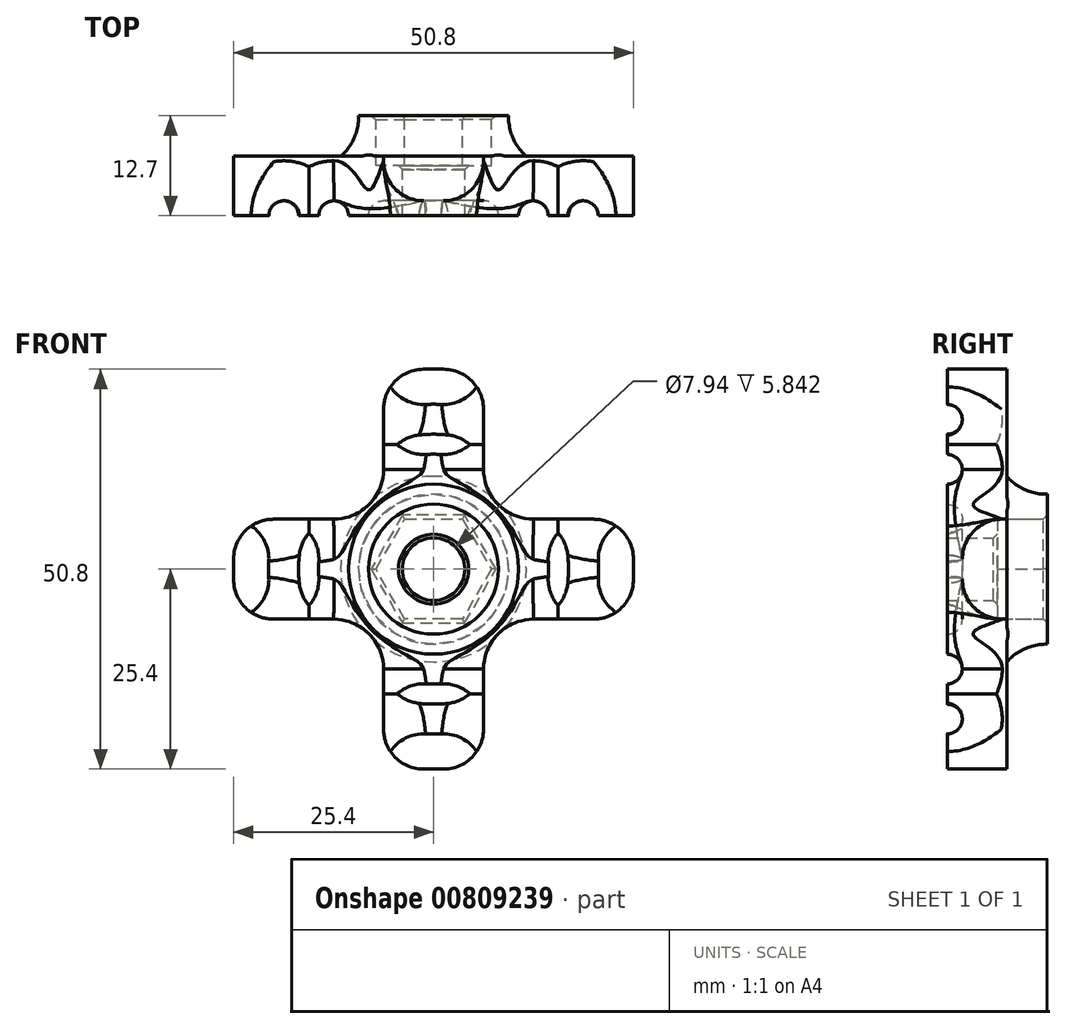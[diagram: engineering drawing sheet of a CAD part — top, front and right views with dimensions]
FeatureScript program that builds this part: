
annotation { "Feature Type Name" : "Feature", "Feature Type Description" : "" }
export const myFeature = defineFeature(function(context is Context, id is Id, definition is map)
    precondition{}
    {
        {
            var Q0;
            Q0=qCreatedBy(makeId("Front.planeOp"),FACE);
            var sketch = newSketch(context, id + "F0", { "sketchPlane" : qUnion([Q0])});
            skCircle(sketch, "E0.cCircle", {"center": v(0, 0) * mm, "radius": 6.35 * mm, "construction": true});
            skLineSegment(sketch, "E0.0", {"start": v(-3.67, 6.35) * mm, "end": v(3.67, 6.35) * mm});
            skLineSegment(sketch, "E0.1", {"start": v(3.67, 6.35) * mm, "end": v(7.33, 0) * mm});
            skLineSegment(sketch, "E0.2", {"start": v(7.33, 0) * mm, "end": v(3.67, -6.35) * mm});
            skLineSegment(sketch, "E0.3", {"start": v(3.67, -6.35) * mm, "end": v(-3.67, -6.35) * mm});
            skLineSegment(sketch, "E0.4", {"start": v(-3.67, -6.35) * mm, "end": v(-7.33, 0) * mm});
            skLineSegment(sketch, "E0.5", {"start": v(-7.33, 0) * mm, "end": v(-3.67, 6.35) * mm});
            skPoint(sketch, "E0.0.midPoint", {"position": v(0, 6.35) * mm});
            skCircle(sketch, "E1", {"center": v(0, 0) * mm, "radius": 3.97 * mm});
            skSolve(sketch);
        }
        {
            var Q0;
            Q0 = qSketchRegion(id + "F0", true);
            extrude(context, id + "F1", {"entities" : qUnion([Q0]), "depth" : 6.35 * mm, "offsetDistance" : 25.4 * mm});
        }
        {
            var Q0;
            Q0=qCreatedBy(makeId("Front.planeOp"),FACE);
            var sketch = newSketch(context, id + "F2", { "sketchPlane" : qUnion([Q0])});
            skLineSegment(sketch, "E2.0.0", {"start": v(-3.67, 6.35) * mm, "end": v(-7.33, 0) * mm});
            skLineSegment(sketch, "E2.0.1", {"start": v(-7.33, 0) * mm, "end": v(-3.67, -6.35) * mm});
            skLineSegment(sketch, "E2.0.2", {"start": v(-3.67, -6.35) * mm, "end": v(3.67, -6.35) * mm});
            skLineSegment(sketch, "E2.0.4", {"start": v(7.33, 0) * mm, "end": v(3.67, 6.35) * mm});
            skLineSegment(sketch, "E2.0.5", {"start": v(3.67, 6.35) * mm, "end": v(-3.67, 6.35) * mm});
            skLineSegment(sketch, "E3", {"start": v(-12.7, 6.35) * mm, "end": v(-20.32, 6.35) * mm});
            skLineSegment(sketch, "E4.MirrorCS", {"start": v(-12.7, -6.35) * mm, "end": v(-20.32, -6.35) * mm});
            skLineSegment(sketch, "E5.MirrorCS", {"start": v(12.7, 6.35) * mm, "end": v(20.32, 6.35) * mm});
            skLineSegment(sketch, "E6.MirrorCS", {"start": v(12.7, -6.35) * mm, "end": v(20.32, -6.35) * mm});
            skLineSegment(sketch, "E7", {"start": v(-6.35, 12.7) * mm, "end": v(-6.35, 20.32) * mm});
            skLineSegment(sketch, "E8.MirrorCS", {"start": v(6.35, 12.7) * mm, "end": v(6.35, 20.32) * mm});
            skLineSegment(sketch, "E9.MirrorCS", {"start": v(-6.35, -12.7) * mm, "end": v(-6.35, -20.32) * mm});
            skLineSegment(sketch, "E10.MirrorCS", {"start": v(6.35, -12.7) * mm, "end": v(6.35, -20.32) * mm});
            skLineSegment(sketch, "E11", {"start": v(-1.27, 25.4) * mm, "end": v(1.27, 25.4) * mm});
            skLineSegment(sketch, "E12", {"start": v(25.4, 1.27) * mm, "end": v(25.4, -1.27) * mm});
            skLineSegment(sketch, "E13", {"start": v(-25.4, 1.27) * mm, "end": v(-25.4, -1.27) * mm});
            skLineSegment(sketch, "E14", {"start": v(-1.27, -25.4) * mm, "end": v(1.27, -25.4) * mm});
            skArc(sketch, "E15", {"start": v(-6.35, -12.7) * mm, "mid": v(-8.2, -8.2) * mm, "end": v(-12.7, -6.35) * mm});
            skArc(sketch, "E16", {"start": v(-12.7, 6.35) * mm, "mid": v(-8.2, 8.2) * mm, "end": v(-6.35, 12.7) * mm});
            skArc(sketch, "E17", {"start": v(6.35, 12.7) * mm, "mid": v(8.2, 8.2) * mm, "end": v(12.7, 6.35) * mm});
            skArc(sketch, "E18", {"start": v(12.7, -6.35) * mm, "mid": v(8.2, -8.2) * mm, "end": v(6.35, -12.7) * mm});
            skPoint(sketch, "E19.MirrorCS.start.orphan", {"position": v(0, 12.7) * mm});
            skLineSegment(sketch, "E20.0.3", {"start": v(3.67, -6.35) * mm, "end": v(7.33, 0) * mm});
            skPoint(sketch, "E21.visualSharp", {"position": v(-25.4, 6.35) * mm});
            skArc(sketch, "E21.filletArc", {"start": v(-20.32, 6.35) * mm, "mid": v(-23.91, 4.86) * mm, "end": v(-25.4, 1.27) * mm});
            skPoint(sketch, "E22.visualSharp", {"position": v(-25.4, -6.35) * mm});
            skArc(sketch, "E22.filletArc", {"start": v(-25.4, -1.27) * mm, "mid": v(-23.91, -4.86) * mm, "end": v(-20.32, -6.35) * mm});
            skPoint(sketch, "E23.visualSharp", {"position": v(-6.35, -25.4) * mm});
            skArc(sketch, "E23.filletArc", {"start": v(-6.35, -20.32) * mm, "mid": v(-4.86, -23.91) * mm, "end": v(-1.27, -25.4) * mm});
            skPoint(sketch, "E24.visualSharp", {"position": v(6.35, -25.4) * mm});
            skArc(sketch, "E24.filletArc", {"start": v(1.27, -25.4) * mm, "mid": v(4.86, -23.91) * mm, "end": v(6.35, -20.32) * mm});
            skPoint(sketch, "E25.visualSharp", {"position": v(25.4, -6.35) * mm});
            skArc(sketch, "E25.filletArc", {"start": v(20.32, -6.35) * mm, "mid": v(23.91, -4.86) * mm, "end": v(25.4, -1.27) * mm});
            skPoint(sketch, "E26.visualSharp", {"position": v(25.4, 6.35) * mm});
            skArc(sketch, "E26.filletArc", {"start": v(25.4, 1.27) * mm, "mid": v(23.91, 4.86) * mm, "end": v(20.32, 6.35) * mm});
            skPoint(sketch, "E27.visualSharp", {"position": v(6.35, 25.4) * mm});
            skArc(sketch, "E27.filletArc", {"start": v(6.35, 20.32) * mm, "mid": v(4.86, 23.91) * mm, "end": v(1.27, 25.4) * mm});
            skPoint(sketch, "E28.visualSharp", {"position": v(-6.35, 25.4) * mm});
            skArc(sketch, "E28.filletArc", {"start": v(-1.27, 25.4) * mm, "mid": v(-4.86, 23.91) * mm, "end": v(-6.35, 20.32) * mm});
            skSolve(sketch);
        }
        {
            var Q0;
            Q0 = qSketchRegion(id + "F2", true);
            extrude(context, id + "F3", {"entities" : qUnion([Q0]), "operationType" : NewBodyOperationType.ADD, "depth" : 6.35 * mm, "offsetDistance" : 25.4 * mm, "hasSecondDirection" : true, "secondDirectionOppositeDirection" : true, "secondDirectionDepth" : 6.35 * mm});
        }
        {
            var Q0;
            Q0=qCreatedBy(makeId("Right.planeOp"),FACE);
            var sketch = newSketch(context, id + "F4", { "sketchPlane" : qUnion([Q0])});
            skPoint(sketch, "E29.0", {"position": v(-6.35, 6.35) * mm});
            skLineSegment(sketch, "E30.0", {"start": v(-6.35, 6.35) * mm, "end": v(-6.35, 12.7) * mm});
            skLineSegment(sketch, "E31.0", {"start": v(-6.35, 12.7) * mm, "end": v(-6.35, 20.32) * mm});
            skLineSegment(sketch, "E32.0", {"start": v(-6.35, 25.4) * mm, "end": v(-6.35, 20.32) * mm});
            skLineSegment(sketch, "E33.0", {"start": v(-6.35, 25.4) * mm, "end": v(6.35, 25.4) * mm});
            skPoint(sketch, "E34.0", {"position": v(-6.35, 0) * mm});
            skLineSegment(sketch, "E35.bottom", {"start": v(0, 25.4) * mm, "end": v(-6.35, 25.4) * mm});
            skLineSegment(sketch, "E35.top", {"start": v(0, 0) * mm, "end": v(-4.45, 0) * mm});
            skLineSegment(sketch, "E35.right", {"start": v(-6.35, 25.4) * mm, "end": v(-6.35, 0) * mm});
            skLineSegment(sketch, "E36.0", {"start": v(-4.45, 19.05) * mm, "end": v(6.35, 19.05) * mm});
            skArc(sketch, "E37", {"start": v(-6.35, 17.15) * mm, "mid": v(-4.45, 19.05) * mm, "end": v(-6.35, 20.96) * mm});
            skArc(sketch, "E38", {"start": v(-6.35, 10.8) * mm, "mid": v(-4.45, 12.7) * mm, "end": v(-6.35, 14.6) * mm});
            skArc(sketch, "E39", {"start": v(-6.35, 4.45) * mm, "mid": v(-4.45, 6.35) * mm, "end": v(-6.35, 8.26) * mm});
            skPoint(sketch, "E40.0", {"position": v(-6.35, 1.27) * mm});
            skCircle(sketch, "E41", {"center": v(-6.35, 0) * mm, "radius": 1.9 * mm});
            skLineSegment(sketch, "E42", {"start": v(-6.35, 20.96) * mm, "end": v(-6.35, -1.9) * mm});
            skSolve(sketch);
        }
        {
            var Q0;
            {var subQ0=sQuery(id+"F4.wireOp",EDGE,"E38");Q0=makeQuery(id+"F4.imprint","IMPRINT",FACE,{"disambiguationData":[TD([[makeQuery(id+"F4.imprint","IMPRINT",EDGE,{"derivedFrom":subQ0}),1.0]])]});}
            var Q1;
            {var subQ0=sQuery(id+"F4.wireOp",EDGE,"E37");var subQ1=makeQuery(id+"F4.imprint","IMPRINT",VERTEX,{"derivedFrom":subQ0});Q1=makeQuery(id+"F4.imprint","IMPRINT",FACE,{"disambiguationData":[TD([[makeQuery(id+"F4.imprint","IMPRINT",EDGE,{"disambiguationData":[TD([[subQ1,1.0]])],"derivedFrom":subQ0}),1.0]])]});}
            var Q2;
            {var subQ0=sQuery(id+"F4.wireOp",EDGE,"E39");Q2=makeQuery(id+"F4.imprint","IMPRINT",FACE,{"disambiguationData":[TD([[makeQuery(id+"F4.imprint","IMPRINT",EDGE,{"derivedFrom":subQ0}),1.0]])]});}
            var Q3;
            Q3=sQuery(id+"F4.wireOp",EDGE,"E35.top");
            revolve(context, id + "F5", {"operationType" : NewBodyOperationType.REMOVE, "surfaceOperationType" : NewSurfaceOperationType.NEW, "entities" : qUnion([Q0, Q1, Q2]), "axis" : qUnion([Q3]), "revolveType" : RevolveType.FULL});
        }
        {
            var Q0;
            Q0=qCreatedBy(makeId("Top.planeOp"),FACE);
            var sketch = newSketch(context, id + "F6", { "sketchPlane" : qUnion([Q0])});
            skPoint(sketch, "E43.0", {"position": v(12.7, 6.35) * mm});
            skLineSegment(sketch, "E44.0", {"start": v(25.4, 1.21) * mm, "end": v(25.4, 6.35) * mm});
            skLineSegment(sketch, "E45.0", {"start": v(12.7, 6.35) * mm, "end": v(20.32, 6.35) * mm});
            skLineSegment(sketch, "E46.0", {"start": v(12.7, 6.35) * mm, "end": v(6.35, 6.35) * mm});
            skLineSegment(sketch, "E47.0.1", {"start": v(6.35, -5.17) * mm, "end": v(6.35, 6.35) * mm});
            skLineSegment(sketch, "E47.0.2", {"start": v(6.35, 6.35) * mm, "end": v(12.7, 6.35) * mm});
            skArc(sketch, "E48", {"start": v(9.52, 6.35) * mm, "mid": v(10.09, 3.53) * mm, "end": v(11.79, 1.21) * mm});
            skLineSegment(sketch, "E49", {"start": v(11.79, 1.21) * mm, "end": v(25.4, 1.21) * mm});
            skLineSegment(sketch, "E50", {"start": v(9.52, 6.35) * mm, "end": v(25.4, 6.35) * mm});
            skPoint(sketch, "E51.orphan", {"position": v(25.4, -6.35) * mm});
            skLineSegment(sketch, "E52.bottom", {"start": v(25.4, 1.21) * mm, "end": v(30.77, 1.21) * mm});
            skLineSegment(sketch, "E52.top", {"start": v(25.4, 9.12) * mm, "end": v(30.77, 9.12) * mm});
            skLineSegment(sketch, "E52.left", {"start": v(25.4, 1.21) * mm, "end": v(25.4, 9.12) * mm});
            skLineSegment(sketch, "E52.right", {"start": v(30.77, 1.21) * mm, "end": v(30.77, 9.12) * mm});
            skSolve(sketch);
        }
        {
            var Q0;
            {var subQ0=sQuery(id+"F6.wireOp",EDGE,"E48");Q0=makeQuery(id+"F6.imprint","IMPRINT",FACE,{"disambiguationData":[TD([[makeQuery(id+"F6.imprint","IMPRINT",EDGE,{"derivedFrom":subQ0}),1.0]])]});}
            var Q1;
            {var subQ3=sQuery(id+"F6.wireOp",EDGE,"E52.bottom");Q1=makeQuery(id+"F6.imprint","IMPRINT",FACE,{"disambiguationData":[TD([[makeQuery(id+"F6.imprint","IMPRINT",EDGE,{"derivedFrom":subQ3}),1.0]])]});}
            var Q2;
            Q2=makeQuery(id+"F1.opExtrude","SWEPT_FACE",FACE,{"disambiguationData":[OSD([sQuery(id+"F0.wireOp",EDGE,"E1")])]});
            revolve(context, id + "F7", {"operationType" : NewBodyOperationType.REMOVE, "surfaceOperationType" : NewSurfaceOperationType.NEW, "entities" : qUnion([Q0, Q1]), "axis" : qUnion([Q2]), "revolveType" : RevolveType.FULL});
        }
        {
            var Q0;
            Q0=makeQuery(id+"F5.boolean.opBoolean","INTERSECT",EDGE,{"derivedFrom":[makeQuery(id+"F3.opExtrude","SWEPT_FACE",FACE,{"disambiguationData":[OSD([sQuery(id+"F2.wireOp",EDGE,"E6.MirrorCS")])]}),makeQuery(id+"F5.opRevolve","SWEPT_FACE",FACE,{"disambiguationData":[OSD([sQuery(id+"F4.wireOp",EDGE,"E37")])]})]});
            var Q1;
            Q1=makeQuery(id+"F5.boolean.opBoolean","INTERSECT",EDGE,{"derivedFrom":[makeQuery(id+"F3.opExtrude","SWEPT_FACE",FACE,{"disambiguationData":[OSD([sQuery(id+"F2.wireOp",EDGE,"E5.MirrorCS")])]}),makeQuery(id+"F5.opRevolve","SWEPT_FACE",FACE,{"disambiguationData":[OSD([sQuery(id+"F4.wireOp",EDGE,"E37")])]})]});
            var Q2;
            Q2=makeQuery(id+"F5.boolean.opBoolean","INTERSECT",EDGE,{"derivedFrom":[makeQuery(id+"F3.opExtrude","SWEPT_FACE",FACE,{"disambiguationData":[OSD([sQuery(id+"F2.wireOp",EDGE,"E18")])]}),makeQuery(id+"F5.opRevolve","SWEPT_FACE",FACE,{"disambiguationData":[OSD([sQuery(id+"F4.wireOp",EDGE,"E38")])]})]});
            var Q3;
            Q3=makeQuery(id+"F5.boolean.opBoolean","INTERSECT",EDGE,{"derivedFrom":[makeQuery(id+"F3.opExtrude","SWEPT_FACE",FACE,{"disambiguationData":[OSD([sQuery(id+"F2.wireOp",EDGE,"E17")])]}),makeQuery(id+"F5.opRevolve","SWEPT_FACE",FACE,{"disambiguationData":[OSD([sQuery(id+"F4.wireOp",EDGE,"E38")])]})]});
            var Q4;
            Q4=makeQuery(id+"F5.boolean.opBoolean","INTERSECT",EDGE,{"derivedFrom":[makeQuery(id+"F3.opExtrude","SWEPT_FACE",FACE,{"disambiguationData":[OSD([sQuery(id+"F2.wireOp",EDGE,"E15")])]}),makeQuery(id+"F5.opRevolve","SWEPT_FACE",FACE,{"disambiguationData":[OSD([sQuery(id+"F4.wireOp",EDGE,"E38")])]})]});
            var Q5;
            Q5=makeQuery(id+"F5.boolean.opBoolean","INTERSECT",EDGE,{"derivedFrom":[makeQuery(id+"F3.opExtrude","SWEPT_FACE",FACE,{"disambiguationData":[OSD([sQuery(id+"F2.wireOp",EDGE,"E4.MirrorCS")])]}),makeQuery(id+"F5.opRevolve","SWEPT_FACE",FACE,{"disambiguationData":[OSD([sQuery(id+"F4.wireOp",EDGE,"E37")])]})]});
            var Q6;
            Q6=makeQuery(id+"F5.boolean.opBoolean","INTERSECT",EDGE,{"derivedFrom":[makeQuery(id+"F3.opExtrude","SWEPT_FACE",FACE,{"disambiguationData":[OSD([sQuery(id+"F2.wireOp",EDGE,"E3")])]}),makeQuery(id+"F5.opRevolve","SWEPT_FACE",FACE,{"disambiguationData":[OSD([sQuery(id+"F4.wireOp",EDGE,"E37")])]})]});
            var Q7;
            Q7=makeQuery(id+"F5.boolean.opBoolean","INTERSECT",EDGE,{"derivedFrom":[makeQuery(id+"F3.opExtrude","SWEPT_FACE",FACE,{"disambiguationData":[OSD([sQuery(id+"F2.wireOp",EDGE,"E7")])]}),makeQuery(id+"F5.opRevolve","SWEPT_FACE",FACE,{"disambiguationData":[OSD([sQuery(id+"F4.wireOp",EDGE,"E37")])]})]});
            var Q8;
            Q8=makeQuery(id+"F5.boolean.opBoolean","INTERSECT",EDGE,{"derivedFrom":[makeQuery(id+"F3.opExtrude","SWEPT_FACE",FACE,{"disambiguationData":[OSD([sQuery(id+"F2.wireOp",EDGE,"E8.MirrorCS")])]}),makeQuery(id+"F5.opRevolve","SWEPT_FACE",FACE,{"disambiguationData":[OSD([sQuery(id+"F4.wireOp",EDGE,"E37")])]})]});
            var Q9;
            Q9=makeQuery(id+"F5.boolean.opBoolean","INTERSECT",EDGE,{"derivedFrom":[makeQuery(id+"F3.opExtrude","SWEPT_FACE",FACE,{"disambiguationData":[OSD([sQuery(id+"F2.wireOp",EDGE,"E16")])]}),makeQuery(id+"F5.opRevolve","SWEPT_FACE",FACE,{"disambiguationData":[OSD([sQuery(id+"F4.wireOp",EDGE,"E38")])]})]});
            var Q10;
            Q10=makeQuery(id+"F5.boolean.opBoolean","INTERSECT",EDGE,{"derivedFrom":[makeQuery(id+"F3.opExtrude","SWEPT_FACE",FACE,{"disambiguationData":[OSD([sQuery(id+"F2.wireOp",EDGE,"E9.MirrorCS")])]}),makeQuery(id+"F5.opRevolve","SWEPT_FACE",FACE,{"disambiguationData":[OSD([sQuery(id+"F4.wireOp",EDGE,"E37")])]})]});
            var Q11;
            Q11=makeQuery(id+"F5.boolean.opBoolean","INTERSECT",EDGE,{"derivedFrom":[makeQuery(id+"F3.opExtrude","SWEPT_FACE",FACE,{"disambiguationData":[OSD([sQuery(id+"F2.wireOp",EDGE,"E10.MirrorCS")])]}),makeQuery(id+"F5.opRevolve","SWEPT_FACE",FACE,{"disambiguationData":[OSD([sQuery(id+"F4.wireOp",EDGE,"E37")])]})]});
            fillet(context, id + "F8", {"entities" : qUnion([Q0, Q1, Q2, Q3, Q4, Q5, Q6, Q7, Q8, Q9, Q10, Q11]), "radius" : 5.08 * mm, "tangentPropagation" : true, "allowEdgeOverflow" : false});
        }
        {
            var Q0;
            Q0=makeQuery(id+"F3.opExtrude","CAP_EDGE",EDGE,{"disambiguationData":[OSD([sQuery(id+"F2.wireOp",EDGE,"E2.0.0")])],"isStart":true});
            var Q1;
            Q1=makeQuery(id+"F3.opExtrude","CAP_EDGE",EDGE,{"disambiguationData":[OSD([sQuery(id+"F2.wireOp",EDGE,"E2.0.2")])],"isStart":true});
            var Q2;
            Q2=makeQuery(id+"F3.opExtrude","CAP_EDGE",EDGE,{"disambiguationData":[OSD([sQuery(id+"F2.wireOp",EDGE,"E20.0.3")])],"isStart":true});
            var Q3;
            Q3=makeQuery(id+"F3.opExtrude","CAP_EDGE",EDGE,{"disambiguationData":[OSD([sQuery(id+"F2.wireOp",EDGE,"E2.0.4")])],"isStart":true});
            var Q4;
            Q4=makeQuery(id+"F1.opExtrude","CAP_EDGE",EDGE,{"disambiguationData":[OSD([sQuery(id+"F0.wireOp",EDGE,"E1")])],"isStart":true});
            var Q5;
            Q5=makeQuery(id+"F3.opExtrude","CAP_EDGE",EDGE,{"disambiguationData":[OSD([sQuery(id+"F2.wireOp",EDGE,"E2.0.1")])],"isStart":true});
            var Q6;
            Q6=makeQuery(id+"F3.opExtrude","CAP_EDGE",EDGE,{"disambiguationData":[OSD([sQuery(id+"F2.wireOp",EDGE,"E2.0.5")])],"isStart":true});
            chamfer(context, id + "F9", {"entities" : qUnion([Q0, Q1, Q2, Q3, Q4, Q5, Q6]), "width" : 0.5 * mm, "tangentPropagation" : true});
        }
    });
